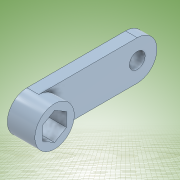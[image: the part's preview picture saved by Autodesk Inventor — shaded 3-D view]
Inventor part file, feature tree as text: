
AUTODESK INVENTOR PART (.ipt)
format: ipt  version: 2022 (Build 260153000, 153)  size: 144,384 bytes
history: native  units: mm
features: extrude x3, sketch x3, other x1
ambient origin geometry x8: Origin, YZ Plane, XZ Plane, XY Plane, X Axis, Y Axis, Z Axis, Center Point
bodies: Body1 (feature_tree)
feature tree (7):
  other  "Sólido1"
  extrude  "Extrusión1"  Depth=10.0mm
  extrude  "Extrusión2"  Depth=4.0mm
  extrude  "Extrusión3"  Depth=4.0mm TaperAngle=0.0deg
  sketch  "Boceto1"  dims[d1=10.0mm d2=10.0mm]
  sketch  "Boceto2"  dims[d3=25.0mm d4=4.0mm]
  sketch  "Boceto3"  dims[d5=3.0mm d6=0.0mm d8=4.0mm d9=0.0mm d10=6.1mm d11=0.0mm d12=0.0mm]
